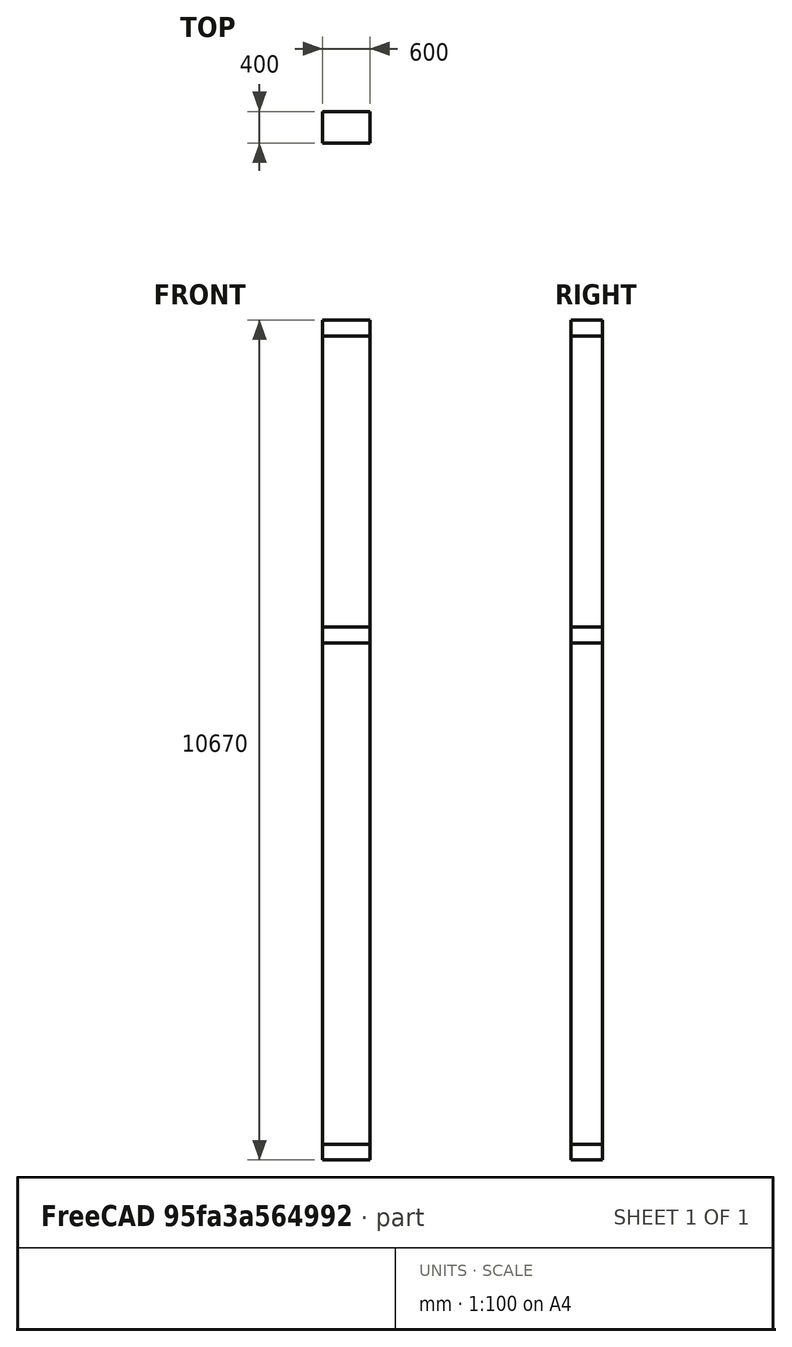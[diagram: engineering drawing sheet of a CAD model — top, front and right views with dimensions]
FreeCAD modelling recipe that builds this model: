
FCSTD DOCUMENT  (FreeCAD 0.21R33694 (Git))
Label: constraint_force_test
License: All rights reserved
LicenseURL: http://en.wikipedia.org/wiki/All_rights_reserved
objects: Part::FeaturePython×7, Part::Plane×5, Fem::ConstraintDisplacement×5, Part::Feature×5, Fem::FemSolverObjectPython×1, App::MaterialObjectPython×1, Part::Box×1, Fem::ConstraintForce×1, Fem::FemMeshObjectPython×1, Fem::FemAnalysis×1
note: 18 computed .brp shape members not serialized (recipe doc carries the construction recipe); baked Part::Feature solids carry a one-line shape summary decoded from their .brp

FEATURE [Fem::FemSolverObjectPython] SolverCcxTools  # FEM object (typed FeaturePython)
  AnalysisType = 0
  BeamShellResultOutput3D = true
  BucklingFactors = 1
  EigenmodeHighLimit = 1000000
  EigenmodeLowLimit = 0
  EigenmodesCount = 10
  GeometricalNonlinearity = 0
  IterationsControlParameterCutb = 0.25,0.5,0.75,0.85,,,1.5,
  IterationsControlParameterIter = 4,8,9,200,10,400,,200,,
  IterationsControlParameterTimeUse = false
  IterationsThermoMechMaximum = 2000
  IterationsUserDefinedIncrementations = false
  IterationsUserDefinedTimeStepLength = false
  MaterialNonlinearity = 0
  MatrixSolverType = 0
  SplitInputWriter = true
  ThermoMechSteadyState = true
  TimeEnd = 1
  TimeInitialStep = 0.01
FEATURE [App::MaterialObjectPython] MaterialSolid  label="steel"  # material (typed FeaturePython)
  Category = 0
  Material = AuthorAndLicense=(c) 2013 Juergen Riegel (CC-BY 3.0),CardName=Steel-Generic,Density=7900 kg/m^3,+9 more (map truncated)
FEATURE [Part::Box] Box  label="Cube"
  AttacherType = Attacher::AttachEngine3D
  Height = 10670
  Length = 600
  Width = 400
FEATURE [Part::Plane] Plane
  AttacherType = Attacher::AttachEngine3D
  Length = 600
  Width = 400
FEATURE [Part::Plane] Plane001
  AttacherType = Attacher::AttachEngine3D
  Length = 600
  Placement = pos=(0,0,200) rot=(0,0,1;0rad)
  Width = 400
FEATURE [Part::Plane] Plane002
  AttacherType = Attacher::AttachEngine3D
  Length = 600
  Placement = pos=(0,0,6570) rot=(0,0,1;0rad)
  Width = 400
FEATURE [Part::Plane] Plane003
  AttacherType = Attacher::AttachEngine3D
  Length = 600
  Placement = pos=(0,0,6770) rot=(0,0,1;0rad)
  Width = 400
FEATURE [Part::Plane] Plane004
  AttacherType = Attacher::AttachEngine3D
  Length = 600
  Placement = pos=(0,0,10470) rot=(0,0,1;0rad)
  Width = 400
FEATURE [Part::FeaturePython] Slice  # WARN: FeaturePython — macro-defined, semantics opaque (R4)
  Base = -> Box
  Mode = 1
  Tolerance = 0
  Tools = -> [Plane,Plane001,Plane002,Plane003,Plane004]
FEATURE [Part::FeaturePython] Slice_child0  label="Slice.0"  # WARN: FeaturePython — macro-defined, semantics opaque (R4)
  Base = -> Slice
  FilterType = 1
  Invert = false
  OverrideMaxVal = 0
  WindowFrom = 80
  WindowTo = 100
  items = 0
FEATURE [Part::FeaturePython] Slice_child1  label="Slice.1"  # WARN: FeaturePython — macro-defined, semantics opaque (R4)
  Base = -> Slice
  FilterType = 1
  Invert = false
  OverrideMaxVal = 0
  WindowFrom = 80
  WindowTo = 100
  items = 1
FEATURE [Part::FeaturePython] Slice_child2  label="Slice.2"  # WARN: FeaturePython — macro-defined, semantics opaque (R4)
  Base = -> Slice
  FilterType = 1
  Invert = false
  OverrideMaxVal = 0
  WindowFrom = 80
  WindowTo = 100
  items = 2
FEATURE [Part::FeaturePython] Slice_child3  label="Slice.3"  # WARN: FeaturePython — macro-defined, semantics opaque (R4)
  Base = -> Slice
  FilterType = 1
  Invert = false
  OverrideMaxVal = 0
  WindowFrom = 80
  WindowTo = 100
  items = 3
FEATURE [Part::FeaturePython] Slice_child4  label="Slice.4"  # WARN: FeaturePython — macro-defined, semantics opaque (R4)
  Base = -> Slice
  FilterType = 1
  Invert = false
  OverrideMaxVal = 0
  WindowFrom = 80
  WindowTo = 100
  items = 4
FEATURE [Fem::ConstraintForce] ConstraintForce  label="wind"
  DirectionVector = (1,0,0)
  Force = 100000
  NormalDirection = (-1,0,0)
  Points = (136) [(0,400,0),(0,400,66.6667),(0,400,133.333),(0,400,200),(0,266.667,0),(0,266.667,66.6667),(0,266.667,133.333),(0,266.667,200),(0,133.333,0),+127 more]
  References = -> [Slice_child0,Slice_child1,Slice_child2,Slice_child3,Slice_child4]
  Reversed = true
  Scale = 19
FEATURE [Fem::ConstraintDisplacement] ConstraintDisplacement  label="top_x"
  NormalDirection = (0,0,1)
  Normals = (4) [(0,0,1),(0,0,1),(0,0,1),(0,0,1)]
  Points = (4) [(600,0,10670),(600,133.333,10670),(600,266.667,10670),(600,400,10670)]
  References = -> [Slice_child4]
  Scale = 22
  hasXFormula = false
  hasYFormula = false
  hasZFormula = false
  rotxFix = false
  rotxFree = true
  rotyFix = false
  rotyFree = true
  rotzFix = false
  rotzFree = true
  useFlowSurfaceForce = false
  xDisplacement = 0
  xFix = false
  xFree = false
  xRotation = 0
  yDisplacement = 0
  yFix = false
  yFree = false
  yRotation = 0
  zDisplacement = 0
  zFix = false
  zFree = true
  zRotation = 0
FEATURE [Fem::ConstraintDisplacement] ConstraintDisplacement001  label="bottom_x"
  NormalDirection = (0,0,1)
  Normals = (4) [(0,0,1),(0,0,1),(0,0,1),(0,0,1)]
  Points = (4) [(600,0,0),(600,133.333,0),(600,266.667,0),(600,400,0)]
  References = -> [Slice_child0]
  Scale = 22
  hasXFormula = false
  hasYFormula = false
  hasZFormula = false
  rotxFix = false
  rotxFree = true
  rotyFix = false
  rotyFree = true
  rotzFix = false
  rotzFree = true
  useFlowSurfaceForce = false
  xDisplacement = 0
  xFix = false
  xFree = false
  xRotation = 0
  yDisplacement = 0
  yFix = false
  yFree = true
  yRotation = 0
  zDisplacement = 0
  zFix = false
  zFree = true
  zRotation = 0
FEATURE [Fem::ConstraintDisplacement] ConstraintDisplacement002  label="bottom_y"
  NormalDirection = (0,0,1)
  Normals = (4) [(0,0,1),(0,0,1),(0,0,1),(0,0,1)]
  Points = (4) [(0,0,0),(200,0,0),(400,0,0),(600,0,0)]
  References = -> [Slice_child0]
  Scale = 26
  hasXFormula = false
  hasYFormula = false
  hasZFormula = false
  rotxFix = false
  rotxFree = true
  rotyFix = false
  rotyFree = true
  rotzFix = false
  rotzFree = true
  useFlowSurfaceForce = false
  xDisplacement = 0
  xFix = false
  xFree = true
  xRotation = 0
  yDisplacement = 0
  yFix = false
  yFree = false
  yRotation = 0
  zDisplacement = 0
  zFix = false
  zFree = true
  zRotation = 0
FEATURE [Fem::ConstraintDisplacement] ConstraintDisplacement003  label="bottom_z"
  NormalDirection = (0,0,-1)
  Normals = (4) [(0,0,-1),(0,0,-1),(0,0,-1),(0,0,-1)]
  Points = (4) [(600,0,0),(600,133.333,0),(600,266.667,0),(600,400,0)]
  References = -> [Slice_child0]
  Scale = 22
  hasXFormula = false
  hasYFormula = false
  hasZFormula = false
  rotxFix = false
  rotxFree = true
  rotyFix = false
  rotyFree = true
  rotzFix = false
  rotzFree = true
  useFlowSurfaceForce = false
  xDisplacement = 0
  xFix = false
  xFree = true
  xRotation = 0
  yDisplacement = 0
  yFix = false
  yFree = true
  yRotation = 0
  zDisplacement = 0
  zFix = false
  zFree = false
  zRotation = 0
FEATURE [Fem::ConstraintDisplacement] ConstraintDisplacement004  label="top_y"
  NormalDirection = (0,0,1)
  Normals = (4) [(0,0,1),(0,0,1),(0,0,1),(0,0,1)]
  Points = (4) [(0,0,10670),(200,0,10670),(400,0,10670),(600,0,10670)]
  References = -> [Slice_child4]
  Scale = 26
  hasXFormula = false
  hasYFormula = false
  hasZFormula = false
  rotxFix = false
  rotxFree = true
  rotyFix = false
  rotyFree = true
  rotzFix = false
  rotzFree = true
  useFlowSurfaceForce = false
  xDisplacement = 0
  xFix = false
  xFree = true
  xRotation = 0
  yDisplacement = 0
  yFix = false
  yFree = false
  yRotation = 0
  zDisplacement = 0
  zFix = false
  zFree = true
  zRotation = 0
FEATURE [Part::Feature] Solid
  shape: bbox 600 x 400 x 200 mm, 6 faces (baked)
FEATURE [Part::Feature] Solid001
  shape: bbox 600 x 400 x 6370 mm, 6 faces (baked)
FEATURE [Part::Feature] Solid002
  shape: bbox 600 x 400 x 200 mm, 6 faces (baked)
FEATURE [Part::Feature] Solid003
  shape: bbox 600 x 400 x 3700 mm, 6 faces (baked)
FEATURE [Part::Feature] Solid004
  shape: bbox 600 x 400 x 200 mm, 6 faces (baked)
FEATURE [Part::FeaturePython] BooleanFragments  # WARN: FeaturePython — macro-defined, semantics opaque (R4)
  Mode = 2
  Objects = -> [Solid,Solid001,Solid002,Solid003,Solid004]
  Tolerance = 0
FEATURE [Fem::FemMeshObjectPython] FEMMeshGmsh  # FEM object (typed FeaturePython)
  Algorithm2D = 0
  Algorithm3D = 0
  CharacteristicLengthMax = 1000
  CharacteristicLengthMin = 0
  CoherenceMesh = true
  ElementDimension = 0
  ElementOrder = 1
  GeometryTolerance = 1e-06
  GroupsOfNodes = false
  HighOrderOptimize = 0
  MeshSizeFromCurvature = 12
  OptimizeNetgen = false
  OptimizeStd = true
  Part = -> BooleanFragments
  RecombinationAlgorithm = 0
  Recombine3DAll = false
  RecombineAll = false
  SecondOrderLinear = false
FEATURE [Fem::FemAnalysis] Analysis
  Group = -> [SolverCcxTools,MaterialSolid,ConstraintForce,ConstraintDisplacement,ConstraintDisplacement001,ConstraintDisplacement002,ConstraintDisplacement003,ConstraintDisplacement004,FEMMeshGmsh]
